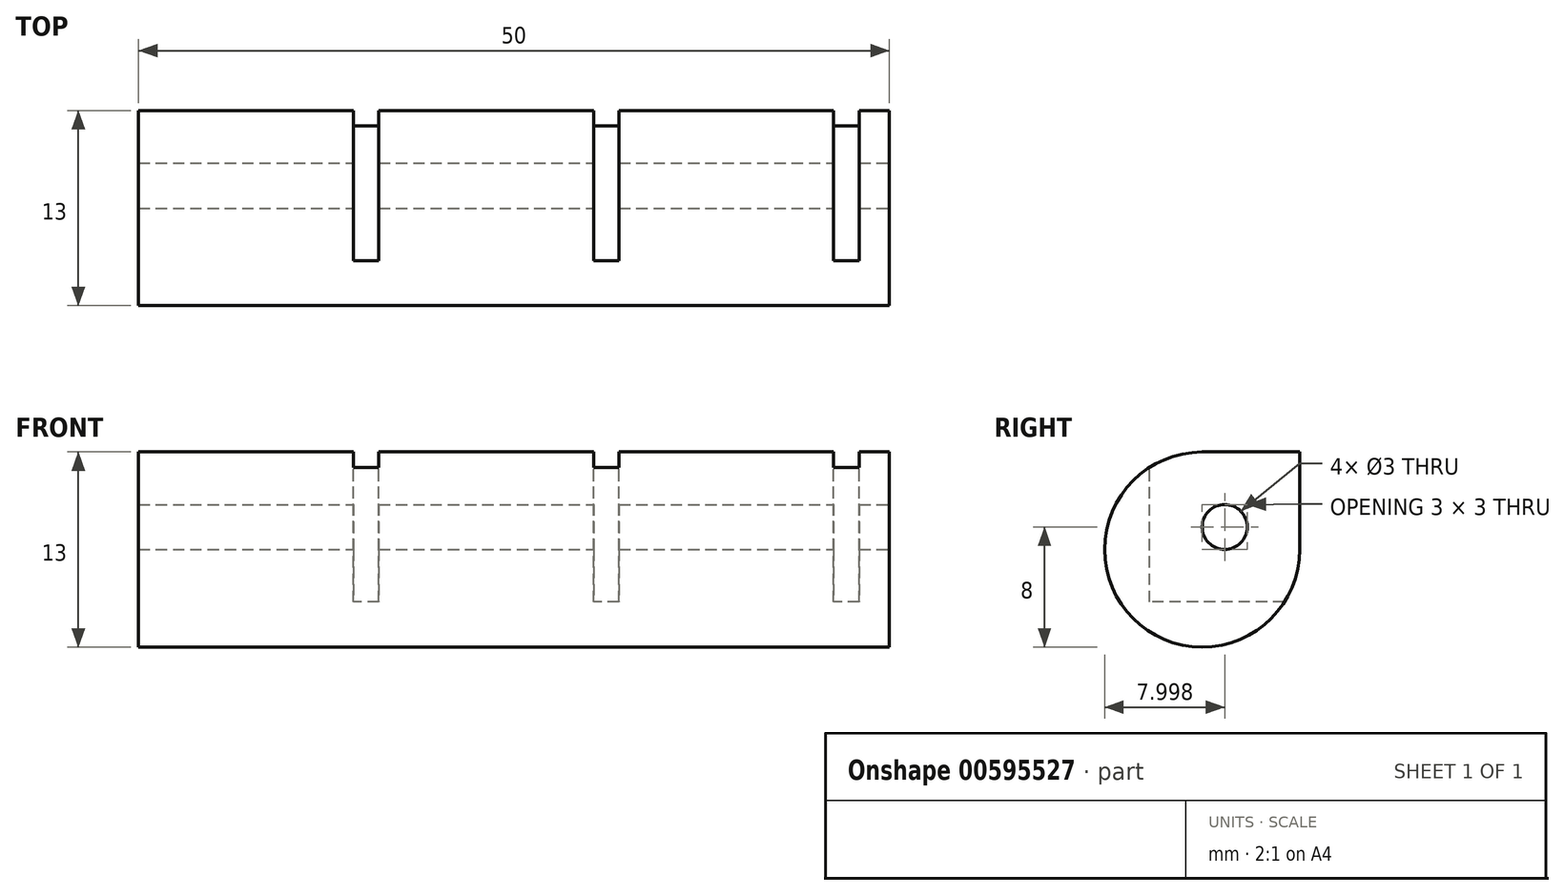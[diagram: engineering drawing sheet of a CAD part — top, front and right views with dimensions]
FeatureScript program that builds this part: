
annotation { "Feature Type Name" : "Feature", "Feature Type Description" : "" }
export const myFeature = defineFeature(function(context is Context, id is Id, definition is map)
    precondition{}
    {
        {
            var Q0;
            Q0=qCreatedBy(makeId("Top.planeOp"),FACE);
            var sketch = newSketch(context, id + "F0", { "sketchPlane" : qUnion([Q0])});
            skLineSegment(sketch, "E0.bottom", {"start": v(-24.14, 5.86) * mm, "end": v(25.86, 5.86) * mm});
            skLineSegment(sketch, "E0.top", {"start": v(-24.14, -7.14) * mm, "end": v(25.86, -7.14) * mm});
            skLineSegment(sketch, "E0.left", {"start": v(-24.14, 5.86) * mm, "end": v(-24.14, -7.14) * mm});
            skLineSegment(sketch, "E0.right", {"start": v(25.86, 5.86) * mm, "end": v(25.86, -7.14) * mm});
            skSolve(sketch);
        }
        {
            var Q0;
            Q0 = qSketchRegion(id + "F0", true);
            var Q1;
            Q1 = qSketchRegion(id + "F2", true);
            extrude(context, id + "F1", {"entities" : qUnion([Q0, Q1]), "depth" : 13 * mm, "offsetDistance" : 25 * mm});
        }
        {
            var Q0;
            Q0=makeQuery(id+"F1.opExtrude","SWEPT_FACE",FACE,{"disambiguationData":[OSD([sQuery(id+"F0.wireOp",EDGE,"E0.right")])]});
            var sketch = newSketch(context, id + "F2", { "sketchPlane" : qUnion([Q0])});
            skCircle(sketch, "E1", {"center": v(0.86, 8) * mm, "radius": 1.5 * mm});
            skLineSegment(sketch, "E2", {"start": v(5.86, 8) * mm, "end": v(0.86, 8) * mm, "construction": true});
            skLineSegment(sketch, "E3", {"start": v(0.86, 8) * mm, "end": v(0.86, 13) * mm, "construction": true});
            skSolve(sketch);
        }
        {
            var Q0;
            Q0=makeQuery(id+"F2.imprint","IMPRINT",FACE,{"disambiguationData":[TD([[makeQuery(id+"F2.imprint","IMPRINT",EDGE,{"derivedFrom":sQuery(id+"F2.wireOp",EDGE,"E1")}),1.0]])]});
            extrude(context, id + "F3", {"entities" : qUnion([Q0]), "operationType" : NewBodyOperationType.REMOVE, "endBound" : BoundingType.THROUGH_ALL, "oppositeDirection" : true, "depth" : 25 * mm, "offsetDistance" : 25 * mm});
        }
        {
            var Q0;
            Q0=makeQuery(id+"F1.opExtrude","CAP_EDGE",EDGE,{"disambiguationData":[OSD([sQuery(id+"F0.wireOp",EDGE,"E0.top")])],"isStart":false});
            var Q1;
            Q1=makeQuery(id+"F1.opExtrude","CAP_EDGE",EDGE,{"disambiguationData":[OSD([sQuery(id+"F0.wireOp",EDGE,"E0.top")])],"isStart":true});
            var Q2;
            Q2=makeQuery(id+"F1.opExtrude","CAP_EDGE",EDGE,{"disambiguationData":[OSD([sQuery(id+"F0.wireOp",EDGE,"E0.bottom")])],"isStart":true});
            fillet(context, id + "F4", {"entities" : qUnion([Q0, Q1, Q2]), "radius" : 6.5 * mm, "tangentPropagation" : true, "allowEdgeOverflow" : false});
        }
        {
            var Q0;
            Q0=makeQuery(id+"F1.opExtrude","CAP_FACE",FACE,{"disambiguationData":[OSD([sQuery(id+"F0.wireOp",EDGE,"E0.bottom"),sQuery(id+"F0.wireOp",EDGE,"E0.top"),sQuery(id+"F0.wireOp",EDGE,"E0.left"),sQuery(id+"F0.wireOp",EDGE,"E0.right")])],"isStart":false});
            var sketch = newSketch(context, id + "F5", { "sketchPlane" : qUnion([Q0])});
            skLineSegment(sketch, "E4.bottom", {"start": v(22.16, 5.86) * mm, "end": v(23.86, 5.86) * mm});
            skLineSegment(sketch, "E4.top", {"start": v(22.16, -4.14) * mm, "end": v(23.86, -4.14) * mm});
            skLineSegment(sketch, "E4.left", {"start": v(22.16, 5.86) * mm, "end": v(22.16, -4.14) * mm});
            skLineSegment(sketch, "E4.right", {"start": v(23.86, 5.86) * mm, "end": v(23.86, -4.14) * mm});
            skLineSegment(sketch, "E5.bottom", {"start": v(6.16, 5.86) * mm, "end": v(7.86, 5.86) * mm});
            skLineSegment(sketch, "E5.top", {"start": v(6.16, -4.14) * mm, "end": v(7.86, -4.14) * mm});
            skLineSegment(sketch, "E5.left", {"start": v(6.16, 5.86) * mm, "end": v(6.16, -4.14) * mm});
            skLineSegment(sketch, "E5.right", {"start": v(7.86, 5.86) * mm, "end": v(7.86, -4.14) * mm});
            skLineSegment(sketch, "E6.bottom", {"start": v(-9.84, 5.86) * mm, "end": v(-8.14, 5.86) * mm});
            skLineSegment(sketch, "E6.top", {"start": v(-9.84, -4.14) * mm, "end": v(-8.14, -4.14) * mm});
            skLineSegment(sketch, "E6.left", {"start": v(-9.84, 5.86) * mm, "end": v(-9.84, -4.14) * mm});
            skLineSegment(sketch, "E6.right", {"start": v(-8.14, 5.86) * mm, "end": v(-8.14, -4.14) * mm});
            skLineSegment(sketch, "E7", {"start": v(-8.14, 5.86) * mm, "end": v(6.16, 5.86) * mm, "construction": true});
            skLineSegment(sketch, "E8", {"start": v(7.86, 5.86) * mm, "end": v(22.16, 5.86) * mm, "construction": true});
            skLineSegment(sketch, "E9", {"start": v(23.86, 5.86) * mm, "end": v(25.86, 5.86) * mm, "construction": true});
            skLineSegment(sketch, "E10", {"start": v(-9.84, 5.86) * mm, "end": v(-24.14, 5.86) * mm, "construction": true});
            skSolve(sketch);
        }
        {
            var Q0;
            Q0 = qSketchRegion(id + "F5", true);
            extrude(context, id + "F6", {"entities" : qUnion([Q0]), "operationType" : NewBodyOperationType.REMOVE, "oppositeDirection" : true, "depth" : 10 * mm, "offsetDistance" : 25 * mm});
        }
    });
